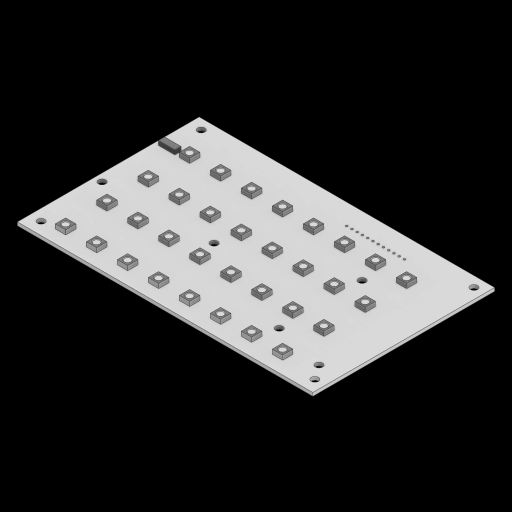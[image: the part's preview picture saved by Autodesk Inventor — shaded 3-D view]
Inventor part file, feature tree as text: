
AUTODESK INVENTOR PART (.ipt)
format: ipt  version: 2024 (Build 280153000, 153)  size: 366,592 bytes
history: native  units: mm
features: extrude x7, sketch x7, pattern_linear x2, chamfer x1, projected_geometry x1
ambient origin geometry x8: Origin, YZ Plane, XZ Plane, XY Plane, X Axis, Y Axis, Z Axis, Center Point
bodies: Volumenkörper1 (feature_tree)
feature tree (18):
  extrude  "Extrusion1"  Depth=88.0mm
  extrude  "Extrusion2"  Depth=1.6mm
  extrude  "Extrusion3"  Depth=6.0mm
  pattern_linear  "Rechteckige Anordnung1"  Spacing1=3.5mm  [1 undecoded]
  extrude  "Extrusion4"  Depth=1.6mm
  extrude  "Extrusion5"  Depth=1.6mm
  chamfer  "Fasen1"  Distance=38.657mm
  pattern_linear  "Rechteckige Anordnung2"  Spacing1=3.5mm  [1 undecoded]
  extrude  "Extrusion6"  Depth=1.6mm
  extrude  "Extrusion7"  Depth=1.6mm
  sketch  "Skizze1"  dims[d0=143.0mm d1=88.0mm]
  sketch  "Skizze2"  dims[d2=1.6mm d3=0.0mm d4=3.5mm]
  sketch  "Skizze3"  dims[d5=83.0mm d6=6.0mm]
  sketch  "Skizze4"  dims[d7=3.5mm]
  sketch  "Skizze5"  dims[d9=3.5mm]
  projected_geometry  "Projizierte Kontur1"
  sketch  "Skizze6"  dims[d10=3.5mm]
  sketch  "Skizze7"  dims[d11=3.5mm d12=3.5mm d13=3.5mm d14=37.25mm d15=38.657mm d16=3.5mm d17=3.75mm d18=3.5mm d19=5.5mm d20=6.0mm d21=56.554mm d22=58.843mm d23=108.0mm d24=108.0mm d25=18.725mm d26=13.0mm d27=133.0mm d28=138.0mm d29=6.0mm d30=138.0mm d31=83.0mm d32=1.6mm d33=0.0mm d34=1.0mm d35=78.0mm d36=81.4mm d37=1.6mm d38=0.0mm d39=120.0mm d41=2.54mm d42=5.0mm d43=5.0mm d44=8.75mm d45=14.625mm d46=2.13mm d47=0.0mm d48=3.6mm d49=0.25mm d50=0.0mm d51=0.25mm d52=2.0mm d53=45.0deg d54=80.0mm d56=15.0mm d57=40.0mm d59=20.0mm d60=0.0mm d61=3.0mm d62=8.0mm d64=6.0mm d65=2.0mm d66=0.0mm d67=125.125mm d68=54.375mm d69=21.0mm d70=51.0mm d71=1.6mm d72=0.0mm]
note: 2 required parameter values undecoded (feature->parameter linkage not recoverable at this tier; creation-order binding heuristic only, values carry confidence <= 0.55)
